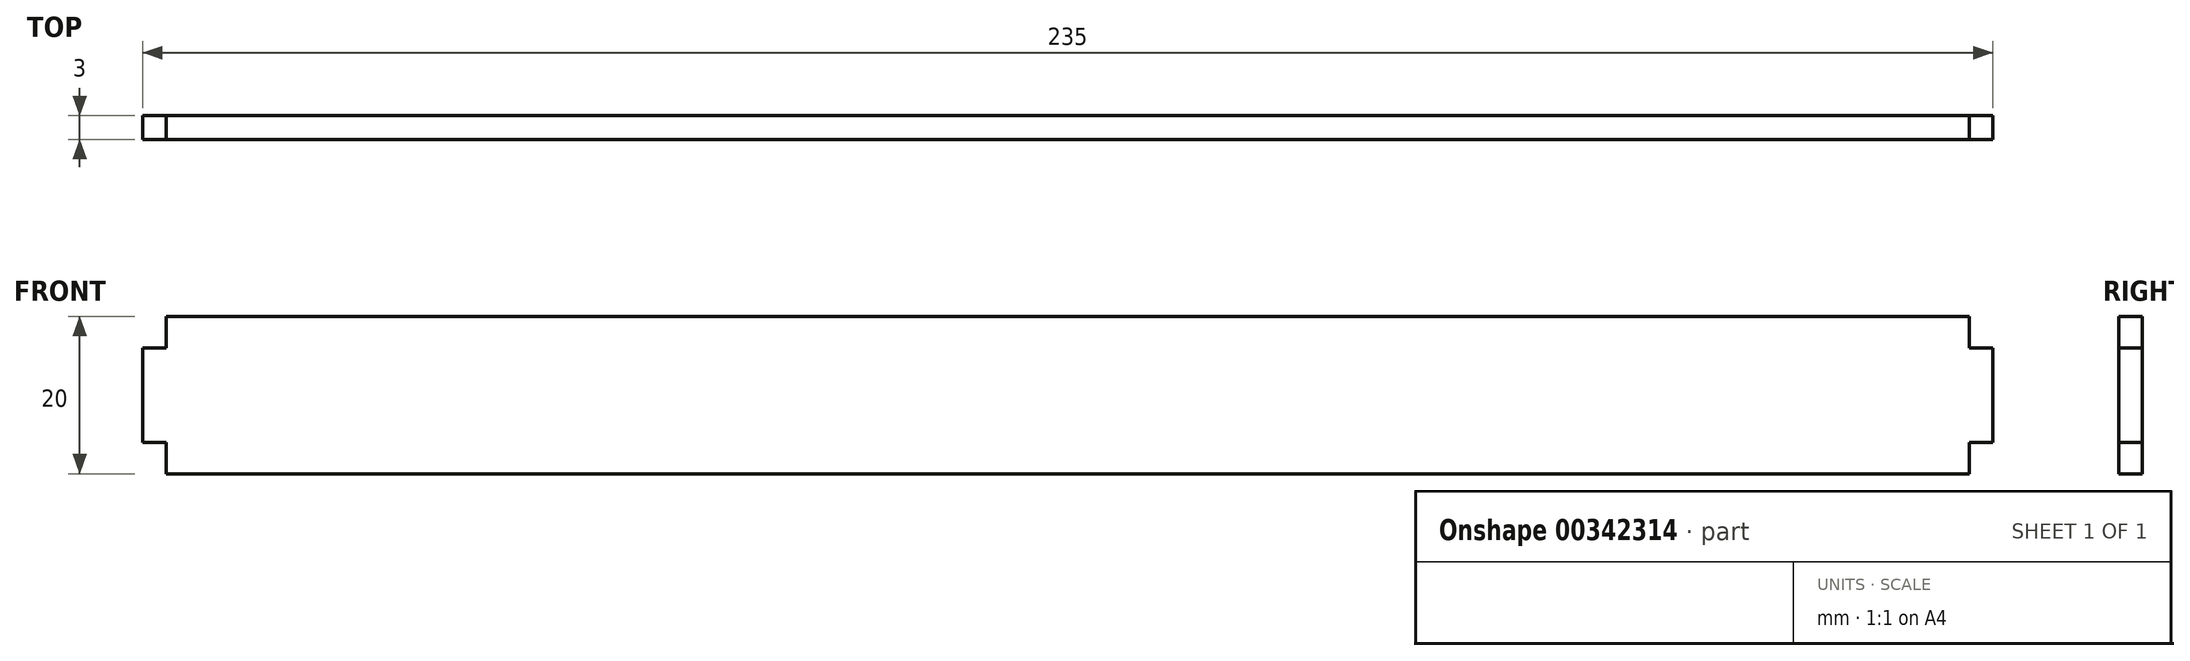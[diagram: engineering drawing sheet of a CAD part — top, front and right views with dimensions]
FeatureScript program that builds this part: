
annotation { "Feature Type Name" : "Feature", "Feature Type Description" : "" }
export const myFeature = defineFeature(function(context is Context, id is Id, definition is map)
    precondition{}
    {
        {
            var Q0;
            Q0=qCreatedBy(makeId("Front.planeOp"),FACE);
            var sketch = newSketch(context, id + "F0", { "sketchPlane" : qUnion([Q0])});
            skLineSegment(sketch, "E0.bottom", {"start": v(0, 0) * mm, "end": v(229, 0) * mm});
            skLineSegment(sketch, "E0.top", {"start": v(0, 20) * mm, "end": v(229, 20) * mm});
            skLineSegment(sketch, "E1.bottom", {"start": v(0, 16) * mm, "end": v(-3, 16) * mm});
            skLineSegment(sketch, "E1.top", {"start": v(0, 4) * mm, "end": v(-3, 4) * mm});
            skLineSegment(sketch, "E1.right", {"start": v(-3, 16) * mm, "end": v(-3, 4) * mm});
            skLineSegment(sketch, "E2.bottom", {"start": v(229, 16) * mm, "end": v(232, 16) * mm});
            skLineSegment(sketch, "E2.top", {"start": v(229, 4) * mm, "end": v(232, 4) * mm});
            skLineSegment(sketch, "E2.right", {"start": v(232, 16) * mm, "end": v(232, 4) * mm});
            skLineSegment(sketch, "E3", {"start": v(0, 20) * mm, "end": v(0, 16) * mm});
            skLineSegment(sketch, "E4", {"start": v(0, 4) * mm, "end": v(0, 0) * mm});
            skLineSegment(sketch, "E5", {"start": v(229, 4) * mm, "end": v(229, 0) * mm});
            skLineSegment(sketch, "E6", {"start": v(229, 16) * mm, "end": v(229, 20) * mm});
            skSolve(sketch);
        }
        {
            var Q0;
            Q0=makeQuery(id+"F0.imprint","IMPRINT",FACE,{"disambiguationData":[TD([[makeQuery(id+"F0.imprint","IMPRINT",EDGE,{"derivedFrom":sQuery(id+"F0.wireOp",EDGE,"E0.bottom")}),1.0]])]});
            extrude(context, id + "F1", {"entities" : qUnion([Q0]), "depth" : 3 * mm, "offsetDistance" : 25 * mm});
        }
    });
